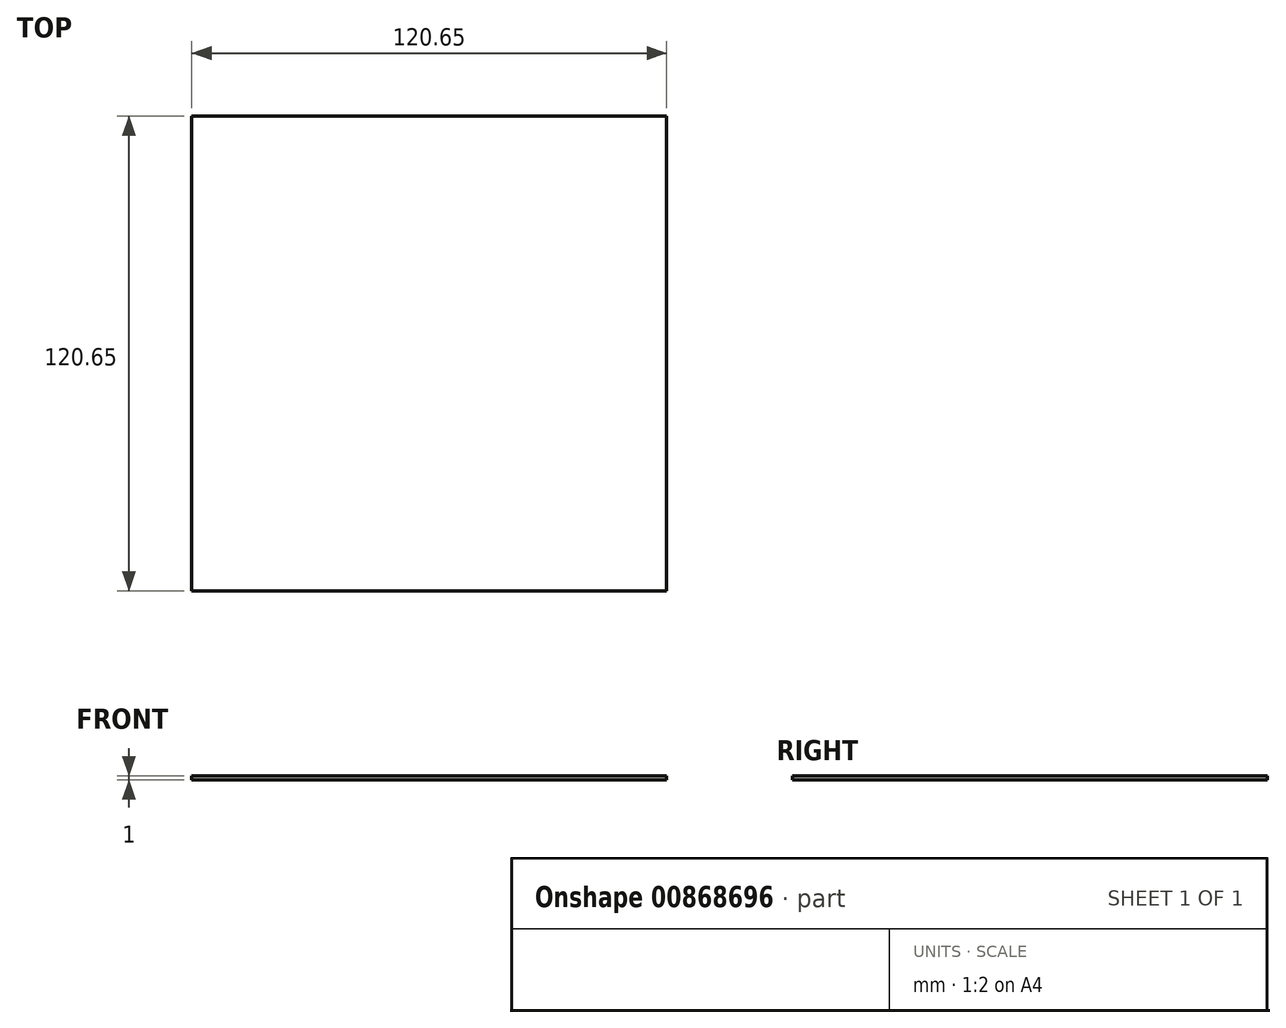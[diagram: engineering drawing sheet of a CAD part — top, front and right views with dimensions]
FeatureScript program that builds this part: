
annotation { "Feature Type Name" : "Feature", "Feature Type Description" : "" }
export const myFeature = defineFeature(function(context is Context, id is Id, definition is map)
    precondition{}
    {
        {
            var Q0;
            Q0=qCreatedBy(makeId("Top.planeOp"),FACE);
            var sketch = newSketch(context, id + "F0", { "sketchPlane" : qUnion([Q0])});
            skLineSegment(sketch, "E0", {"start": v(-127, 56.15) * mm, "end": v(-6.35, 56.15) * mm});
            skLineSegment(sketch, "E1", {"start": v(-6.35, 56.15) * mm, "end": v(-6.35, 11.7) * mm});
            skLineSegment(sketch, "E2", {"start": v(-6.35, 11.7) * mm, "end": v(-6.35, 11.7) * mm});
            skLineSegment(sketch, "E3", {"start": v(-6.35, 11.7) * mm, "end": v(-6.35, -64.5) * mm});
            skLineSegment(sketch, "E4", {"start": v(-6.35, -64.5) * mm, "end": v(-127, -64.5) * mm});
            skLineSegment(sketch, "E5", {"start": v(-127, -64.5) * mm, "end": v(-127, 11.7) * mm});
            skLineSegment(sketch, "E6", {"start": v(-127, 11.7) * mm, "end": v(-127, 11.7) * mm});
            skLineSegment(sketch, "E7", {"start": v(-127, 11.7) * mm, "end": v(-127, 56.15) * mm});
            skSolve(sketch);
        }
        {
            var Q0;
            Q0=makeQuery(id+"F0.imprint","IMPRINT",FACE,{"disambiguationData":[TD([[makeQuery(id+"F0.imprint","IMPRINT",EDGE,{"derivedFrom":sQuery(id+"F0.wireOp",EDGE,"ULd2588Q-JHcO-3Ezt-B4LH-CQlkXiQgMfxx.bottom")}),-1.0]])]});
            var Q1;
            Q1=makeQuery(id+"F0.imprint","IMPRINT",FACE,{"disambiguationData":[TD([[makeQuery(id+"F0.imprint","IMPRINT",EDGE,{"derivedFrom":sQuery(id+"F0.wireOp",EDGE,"E0")}),-1.0]])]});
            extrude(context, id + "F1", {"entities" : qUnion([Q0, Q1]), "depth" : 1 * mm, "offsetDistance" : 25.4 * mm});
        }
    });
